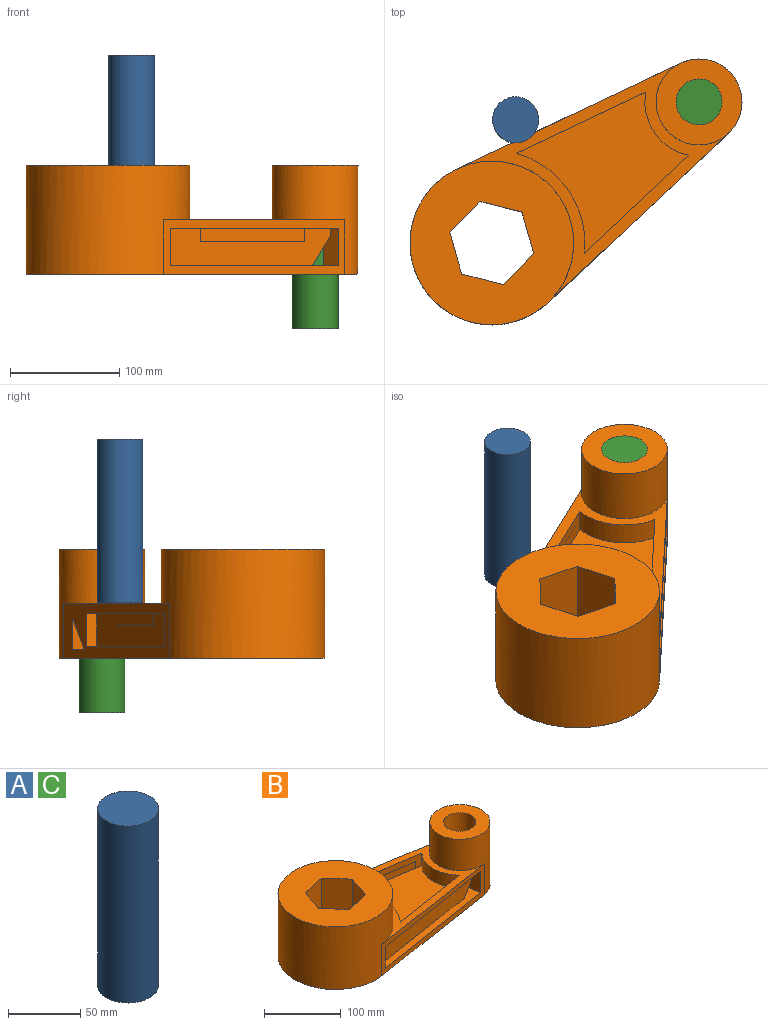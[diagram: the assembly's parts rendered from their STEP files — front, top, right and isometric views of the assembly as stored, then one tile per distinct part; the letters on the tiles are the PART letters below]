
ASSEMBLY  parts=3 mates=1
PART A: 3 faces, bbox 42.1x42.1x150 mm
  f0: cylinder r=21.07mm len=150mm, axis (0,0,-1), area 19855.4mm2, adj f1,f2
  f1: plane 42.13x42.13mm, normal (0,0,1), area 1394.3mm2, adj f0
  f2: plane 42.13x42.13mm, normal (0,0,-1), area 1394.3mm2, adj f0
PART B: 33 faces, bbox 344.2x150x100 mm
  f0: plane 331.53x150mm, normal (0,0,-1), area 31589.5mm2, adj f2,f3,f5,f6,f7,f9,f27,f28
  f1: plane 150x150mm, normal (0,0,1), area 13587.4mm2, adj f7,f27,f28,f29,f30,f31,f32
  f2: cylinder r=21.07mm len=100mm, axis (0,0,1), area 12370.2mm2, adj f0,f8,f15,f18,f25,f26
  f3: plane 224.26x50mm, normal (0.16,-0.99,0), area 4119.4mm2, adj f0,f4,f5,f7,f15,f16,f17,f18
  f4: plane 224.26x148.19mm, normal (0,0,1), area 5846.1mm2, adj f3,f5,f6,f7,f10,f11,f12,f13
  f5: cylinder r=39.37mm len=100mm, axis (0,0,1), area 16885.9mm2, adj f0,f3,f4,f6,f8,f9
  f6: plane 224.26x50mm, normal (0.16,0.99,0), area 6085.8mm2, adj f0,f4,f5,f7,f18,f20,f21,f22
  f7: cylinder r=75mm len=150mm, axis (0,0,1), area 36510.4mm2, adj f0,f1,f3,f4,f6
  f8: plane 78.75x78.75mm, normal (0,0,1), area 3476.2mm2, adj f2,f5
  f9: plane 64.59x22.76mm, normal (0.76,0.12,-0.64), area 1250.4mm2, adj f0,f5
  f10: plane 129.76x20.36mm, normal (-0.16,-0.99,0), area 2626.9mm2, adj f4,f11,f13,f14
  f11: cylinder r=85.26mm len=110.72mm, axis (0,0,1), area 2410.1mm2, adj f4,f10,f12,f14
  f12: plane 129.76x20.36mm, normal (-0.16,0.99,0), area 2626.9mm2, adj f4,f11,f13,f14
  f13: cylinder r=49.63mm len=69.99mm, axis (0,0,1), area 1553.7mm2, adj f4,f10,f12,f14
  f14: plane 129.76x110.72mm, normal (0,0,1), area 9481mm2, adj f10,f11,f12,f13
  f15: plane 34.23x19.6mm, normal (-0.99,-0.16,0), area 613.8mm2, adj f2,f3,f16,f18,f19,f25
  f16: plane 210.24x42.63mm, normal (0,0,-1), area 2112.4mm2, adj f3,f15,f17,f19
  f17: plane 34.23x9.88mm, normal (0.99,0.16,0), area 342.3mm2, adj f3,f16,f18,f19
  f18: plane 210.24x118.77mm, normal (0,0,1), area 3512.7mm2, adj f2,f3,f6,f15,f17,f19,f25,f26
  f19: plane 208.68x34.23mm, normal (0.16,-0.99,0), area 6913.2mm2, adj f15,f16,f17,f18,f25
  f20: plane 166.93x35.83mm, normal (0,0,-1), area 1674.1mm2, adj f6,f21,f23,f24
  f21: plane 29.45x9.88mm, normal (-0.99,0.16,0), area 294.5mm2, adj f6,f20,f22,f24
  f22: plane 166.93x35.83mm, normal (0,0,1), area 1674.1mm2, adj f6,f21,f23,f24
  f23: plane 29.45x9.88mm, normal (0.99,-0.16,0), area 294.5mm2, adj f6,f20,f22,f24
  f24: plane 165.38x29.45mm, normal (0.16,0.99,0), area 4930.7mm2, adj f20,f21,f22,f23
  f25: plane 79.71x35.27mm, normal (0.76,0.12,-0.64), area 2185.2mm2, adj f2,f6,f15,f18,f19,f26
  f26: plane 27.59x24.07mm, normal (-0.99,-0.16,0), area 672.3mm2, adj f2,f6,f18,f25
  f27: plane 100x37.64mm, normal (-0.95,0.31,0), area 3964.8mm2, adj f0,f1,f28,f32
  f28: plane 100x29.61mm, normal (-0.75,-0.67,0), area 3964.8mm2, adj f0,f1,f27,f29
  f29: plane 100x38.83mm, normal (0.2,-0.98,0), area 3964.8mm2, adj f0,f1,f28,f30
  f30: plane 100x37.64mm, normal (0.95,-0.31,0), area 3964.8mm2, adj f0,f1,f29,f31
  f31: plane 100x29.61mm, normal (0.75,0.67,0), area 3964.8mm2, adj f0,f1,f30,f32
  f32: plane 100x38.83mm, normal (-0.2,0.98,0), area 3964.8mm2, adj f0,f1,f27,f31
PART C: same geometry as A
PLACE A rot(axis=(0,0,1),34.2deg) t=(-37.61,-36.24,-99.28)mm
PLACE B rot(axis=(0,0,1),34.2deg) t=(-59.42,-149.05,-100.32)mm fixed
PLACE C rot(axis=(0,0,1),34.2deg) t=(130.53,-19.73,-200.32)mm
MATE fastened C.f0 <-> B.f2  axis (0,0,1) through (130.53,-19.73,-50.32)mm
